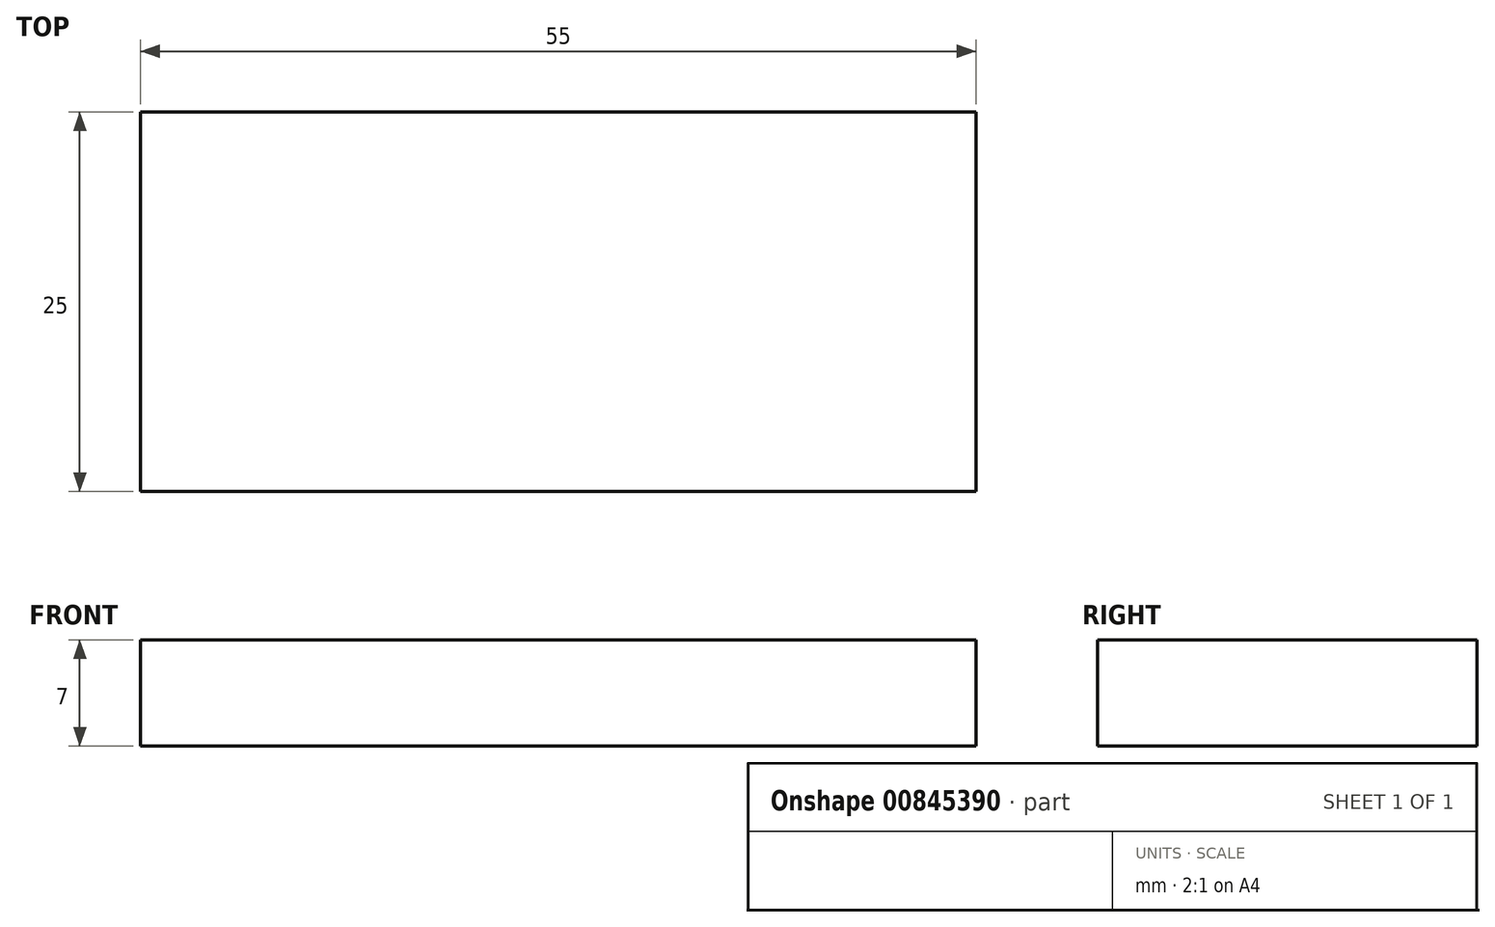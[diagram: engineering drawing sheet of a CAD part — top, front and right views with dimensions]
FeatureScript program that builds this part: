
annotation { "Feature Type Name" : "Feature", "Feature Type Description" : "" }
export const myFeature = defineFeature(function(context is Context, id is Id, definition is map)
    precondition{}
    {
        {
            var Q0;
            Q0=qCreatedBy(makeId("Top.planeOp"),FACE);
            var sketch = newSketch(context, id + "F0", { "sketchPlane" : qUnion([Q0])});
            skLineSegment(sketch, "E0.bottom", {"start": v(-27.5, 12.5) * mm, "end": v(27.5, 12.5) * mm});
            skLineSegment(sketch, "E0.top", {"start": v(-27.5, -12.5) * mm, "end": v(27.5, -12.5) * mm});
            skLineSegment(sketch, "E0.left", {"start": v(-27.5, 12.5) * mm, "end": v(-27.5, -12.5) * mm});
            skLineSegment(sketch, "E0.right", {"start": v(27.5, 12.5) * mm, "end": v(27.5, -12.5) * mm});
            skPoint(sketch, "E0.middle", {"position": v(0, 0) * mm});
            skSolve(sketch);
        }
        {
            var Q0;
            Q0=makeQuery(id+"F0.imprint","IMPRINT",FACE,{"disambiguationData":[TD([[makeQuery(id+"F0.imprint","IMPRINT",EDGE,{"derivedFrom":sQuery(id+"F0.wireOp",EDGE,"E0.bottom")}),-1.0]])]});
            extrude(context, id + "F1", {"entities" : qUnion([Q0]), "depth" : 7 * mm, "offsetDistance" : 25 * mm});
        }
    });
